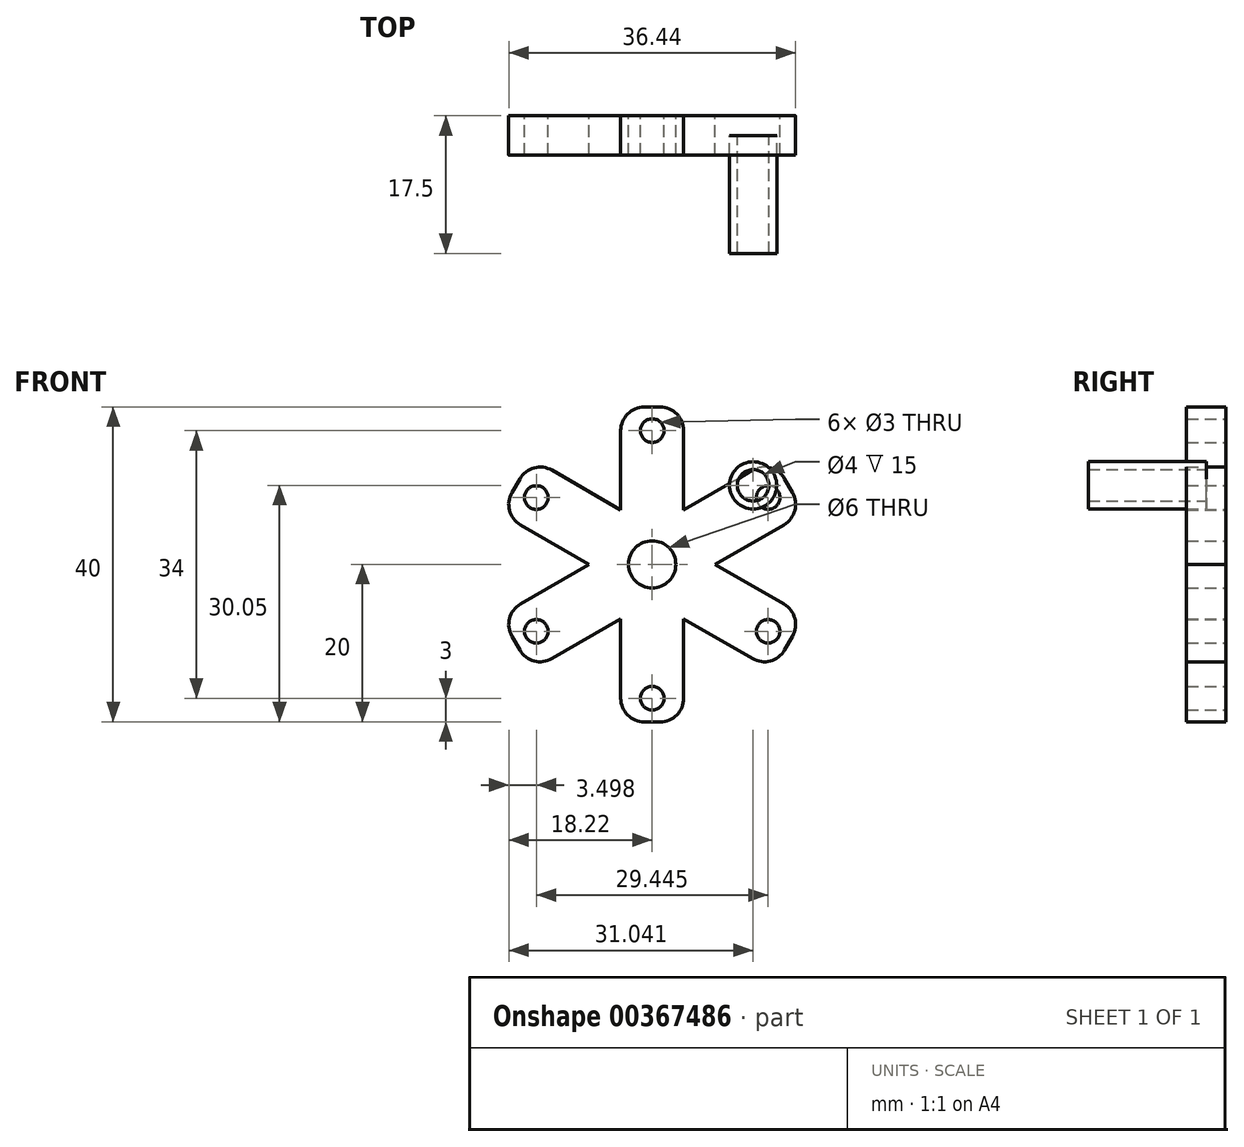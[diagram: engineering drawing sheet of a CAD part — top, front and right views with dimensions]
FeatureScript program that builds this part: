
annotation { "Feature Type Name" : "Feature", "Feature Type Description" : "" }
export const myFeature = defineFeature(function(context is Context, id is Id, definition is map)
    precondition{}
    {
        {
            var Q0;
            Q0=qCreatedBy(makeId("Front.planeOp"),FACE);
            var sketch = newSketch(context, id + "F0", { "sketchPlane" : qUnion([Q0])});
            skLineSegment(sketch, "E0.left", {"start": v(4, 17) * mm, "end": v(4, 6.93) * mm});
            skLineSegment(sketch, "E0.right", {"start": v(-4, 17) * mm, "end": v(-4, 6.93) * mm});
            skPoint(sketch, "E0.middle", {"position": v(0, 0) * mm});
            skPoint(sketch, "E1.orphan", {"position": v(-10, 0) * mm});
            skPoint(sketch, "E0.top.end.orphan", {"position": v(-4, -20) * mm});
            skPoint(sketch, "E0.top.start.orphan", {"position": v(4, -20) * mm});
            skCircle(sketch, "E2", {"center": v(0, 17) * mm, "radius": 1.5 * mm});
            skPoint(sketch, "E3.visualSharp", {"position": v(-4, 20) * mm});
            skArc(sketch, "E3.filletArc", {"start": v(-1, 20) * mm, "mid": v(-3.12, 19.12) * mm, "end": v(-4, 17) * mm});
            skPoint(sketch, "E4.visualSharp", {"position": v(4, 20) * mm});
            skArc(sketch, "E4.filletArc", {"start": v(4, 17) * mm, "mid": v(3.12, 19.12) * mm, "end": v(1, 20) * mm});
            skPoint(sketch, "E5.orphan", {"position": v(2, 3.46) * mm});
            skPoint(sketch, "E6.orphan", {"position": v(-2, 3.46) * mm});
            skPoint(sketch, "E7.orphan", {"position": v(-4, 0) * mm});
            skPoint(sketch, "E8.orphan", {"position": v(4, 0) * mm});
            skPoint(sketch, "E9.orphan", {"position": v(2, -3.46) * mm});
            skPoint(sketch, "E10.orphan", {"position": v(-2, -3.46) * mm});
            skCircle(sketch, "E11", {"center": v(0, 0) * mm, "radius": 3 * mm});
            skLineSegment(sketch, "E12", {"start": v(-1, 20) * mm, "end": v(1, 20) * mm});
            skLineSegment(sketch, "E13.1.0", {"start": v(-12.72, 11.96) * mm, "end": v(-4, 6.93) * mm});
            skArc(sketch, "E13.1.1", {"start": v(-12.72, 11.96) * mm, "mid": v(-15, 12.26) * mm, "end": v(-16.82, 10.87) * mm});
            skArc(sketch, "E13.1.2", {"start": v(-17.82, 9.13) * mm, "mid": v(-18.12, 6.86) * mm, "end": v(-16.72, 5.04) * mm});
            skLineSegment(sketch, "E13.1.3", {"start": v(-17.82, 9.13) * mm, "end": v(-16.82, 10.87) * mm});
            skLineSegment(sketch, "E13.1.4", {"start": v(-16.72, 5.04) * mm, "end": v(-8, 0) * mm});
            skCircle(sketch, "E13.1.5", {"center": v(-14.72, 8.5) * mm, "radius": 1.5 * mm});
            skLineSegment(sketch, "E13.2.0", {"start": v(-16.72, -5.04) * mm, "end": v(-8, 0) * mm});
            skArc(sketch, "E13.2.1", {"start": v(-16.72, -5.04) * mm, "mid": v(-18.12, -6.86) * mm, "end": v(-17.82, -9.13) * mm});
            skArc(sketch, "E13.2.2", {"start": v(-16.82, -10.87) * mm, "mid": v(-15, -12.26) * mm, "end": v(-12.72, -11.96) * mm});
            skLineSegment(sketch, "E13.2.3", {"start": v(-16.82, -10.87) * mm, "end": v(-17.82, -9.13) * mm});
            skLineSegment(sketch, "E13.2.4", {"start": v(-12.72, -11.96) * mm, "end": v(-4, -6.93) * mm});
            skCircle(sketch, "E13.2.5", {"center": v(-14.72, -8.5) * mm, "radius": 1.5 * mm});
            skLineSegment(sketch, "E13.3.0", {"start": v(-4, -17) * mm, "end": v(-4, -6.93) * mm});
            skArc(sketch, "E13.3.1", {"start": v(-4, -17) * mm, "mid": v(-3.12, -19.12) * mm, "end": v(-1, -20) * mm});
            skArc(sketch, "E13.3.2", {"start": v(1, -20) * mm, "mid": v(3.12, -19.12) * mm, "end": v(4, -17) * mm});
            skLineSegment(sketch, "E13.3.3", {"start": v(1, -20) * mm, "end": v(-1, -20) * mm});
            skLineSegment(sketch, "E13.3.4", {"start": v(4, -17) * mm, "end": v(4, -6.93) * mm});
            skCircle(sketch, "E13.3.5", {"center": v(0, -17) * mm, "radius": 1.5 * mm});
            skLineSegment(sketch, "E13.4.0", {"start": v(12.72, -11.96) * mm, "end": v(4, -6.93) * mm});
            skArc(sketch, "E13.4.1", {"start": v(12.72, -11.96) * mm, "mid": v(15, -12.26) * mm, "end": v(16.82, -10.87) * mm});
            skArc(sketch, "E13.4.2", {"start": v(17.82, -9.13) * mm, "mid": v(18.12, -6.86) * mm, "end": v(16.72, -5.04) * mm});
            skLineSegment(sketch, "E13.4.3", {"start": v(17.82, -9.13) * mm, "end": v(16.82, -10.87) * mm});
            skLineSegment(sketch, "E13.4.4", {"start": v(16.72, -5.04) * mm, "end": v(8, 0) * mm});
            skCircle(sketch, "E13.4.5", {"center": v(14.72, -8.5) * mm, "radius": 1.5 * mm});
            skLineSegment(sketch, "E13.5.0", {"start": v(16.72, 5.04) * mm, "end": v(8, 0) * mm});
            skArc(sketch, "E13.5.1", {"start": v(16.72, 5.04) * mm, "mid": v(18.12, 6.86) * mm, "end": v(17.82, 9.13) * mm});
            skArc(sketch, "E13.5.2", {"start": v(16.82, 10.87) * mm, "mid": v(15, 12.26) * mm, "end": v(12.72, 11.96) * mm});
            skLineSegment(sketch, "E13.5.3", {"start": v(16.82, 10.87) * mm, "end": v(17.82, 9.13) * mm});
            skLineSegment(sketch, "E13.5.4", {"start": v(12.72, 11.96) * mm, "end": v(4, 6.93) * mm});
            skCircle(sketch, "E13.5.5", {"center": v(14.72, 8.5) * mm, "radius": 1.5 * mm});
            skPoint(sketch, "E14.orphan", {"position": v(0, -4.62) * mm});
            skPoint(sketch, "E15.orphan", {"position": v(4, -2.3) * mm});
            skPoint(sketch, "E16.orphan", {"position": v(4, 2.3) * mm});
            skPoint(sketch, "E17.orphan", {"position": v(0, 4.62) * mm});
            skPoint(sketch, "E18.orphan", {"position": v(-4, 2.3) * mm});
            skPoint(sketch, "E19.orphan", {"position": v(-4, -2.3) * mm});
            skSolve(sketch);
        }
        {
            var Q0;
            Q0=makeQuery(id+"F0.imprint","IMPRINT",FACE,{"disambiguationData":[TD([[makeQuery(id+"F0.imprint","IMPRINT",EDGE,{"derivedFrom":sQuery(id+"F0.wireOp",EDGE,"E0.left")}),-1.0]])]});
            extrude(context, id + "F1", {"entities" : qUnion([Q0]), "endBound" : BoundingType.SYMMETRIC, "depth" : 5 * mm});
        }
        {
            var Q0;
            Q0=qCreatedBy(makeId("Front.planeOp"),FACE);
            var sketch = newSketch(context, id + "F2", { "sketchPlane" : qUnion([Q0])});
            skCircle(sketch, "E20", {"center": v(-21.39, 23.64) * mm, "radius": 4.5 * mm});
            skCircle(sketch, "E21", {"center": v(-21.39, 23.64) * mm, "radius": 3 * mm});
            skSolve(sketch);
        }
        {
            var Q0;
            Q0=makeQuery(id+"F2.imprint","IMPRINT",FACE,{"disambiguationData":[TD([[makeQuery(id+"F2.imprint","IMPRINT",EDGE,{"derivedFrom":sQuery(id+"F2.wireOp",EDGE,"E20")}),1.0]])]});
            extrude(context, id + "F3", {"entities" : qUnion([Q0]), "depth" : 5.5 * mm});
        }
        {
            var Q0;
            Q0=makeQuery(id+"F3.opExtrude","SWEPT_BODY",BODY,{"disambiguationData":[OSD([sQuery(id+"F2.wireOp",EDGE,"E20"),sQuery(id+"F2.wireOp",EDGE,"E21")])]});
            deleteBodies(context, id + "F4", {"entities" : qUnion([Q0])});
        }
        {
            var Q0;
            Q0=qCreatedBy(makeId("Front.planeOp"),FACE);
            var sketch = newSketch(context, id + "F5", { "sketchPlane" : qUnion([Q0])});
            skCircle(sketch, "E22", {"center": v(12.82, 10.05) * mm, "radius": 3 * mm});
            skCircle(sketch, "E23", {"center": v(12.82, 10.05) * mm, "radius": 2 * mm});
            skSolve(sketch);
        }
        {
            var Q0;
            Q0=makeQuery(id+"F5.imprint","IMPRINT",FACE,{"disambiguationData":[TD([[makeQuery(id+"F5.imprint","IMPRINT",EDGE,{"derivedFrom":sQuery(id+"F5.wireOp",EDGE,"E22")}),1.0]])]});
            extrude(context, id + "F6", {"entities" : qUnion([Q0]), "depth" : 15 * mm});
        }
    });
